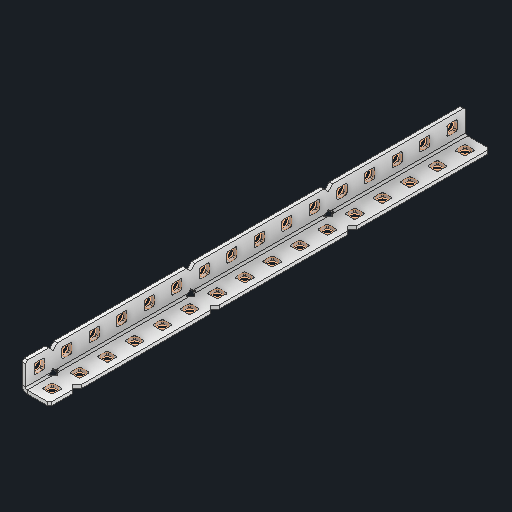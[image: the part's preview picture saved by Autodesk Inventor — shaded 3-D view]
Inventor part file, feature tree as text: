
AUTODESK INVENTOR PART (.ipt)
format: ipt  version: 2025 (Build 290162000, 162)  size: 732,160 bytes
history: native  units: in
note: dims shown in document units (in); Inventor stores cm internally (conversion verified against a paired STEP export)
features: other x73, sketch x2, sheet_metal_op x1
ambient origin geometry x8: Origin, YZ Plane, XZ Plane, XY Plane, X Axis, Y Axis, Z Axis, Center Point
bodies: Solid1 (feature_tree)
feature tree (76):
  other  "Alu Angle 1x1x16.ipt"
  other  "Solid1::Alu Angle 1x1x16.ipt"
  other  "TaggingFeature1"
  sketch  "Sketch1"  dims[d0=0.3937in]
  sketch  "Sketch2"  dims[d1=0.0625in]
  sheet_metal_op  "Body Pattern Sketch"
  other  "Arc Length"
  other  "Diagonal Plane"
  other  "Srf1"
  other  "Srf2"
  other  "Srf3"
  other  "Srf4"
  other  "Srf5"
  other  "Srf6"
  other  "Srf7"
  other  "Srf8"
  other  "Srf9"
  other  "Srf10"
  other  "Srf11"
  other  "Srf12"
  other  "Srf13"
  other  "Srf14"
  other  "Srf15"
  other  "Srf16"
  other  "Srf17"
  other  "Srf18"
  other  "Srf19"
  other  "Srf20"
  other  "Srf21"
  other  "Srf22"
  other  "Srf23"
  other  "Srf24"
  other  "Srf25"
  other  "Srf26"
  other  "Srf27"
  other  "Srf28"
  other  "Srf29"
  other  "Srf30"
  other  "Srf31"
  other  "Srf32"
  other  "Srf33"
  other  "Srf34"
  other  "Srf91::Derived"
  other  "Srf92::Derived"
  other  "Srf856::Derived"
  other  "Srf857::Derived"
  other  "Srf858::Derived"
  other  "Srf859::Derived"
  other  "Srf860::Derived"
  other  "Srf861::Derived"
  other  "Srf1383::Derived"
  other  "Srf1384::Derived"
  other  "Srf1385::Derived"
  other  "Srf1386::Derived"
  other  "Srf1387::Derived"
  other  "Srf1388::Derived"
  other  "Srf1389::Derived"
  other  "Srf1390::Derived"
  other  "Srf1391::Derived"
  other  "Srf1275::Derived"
  other  "Srf1276::Derived"
  other  "Srf1278::Derived"
  other  "Srf1279::Derived"
  other  "Srf1280::Derived"
  other  "Srf1281::Derived"
  other  "Srf1282::Derived"
  other  "Srf1283::Derived"
  other  "Srf1475::Derived"
  other  "Srf1476::Derived"
  other  "Srf1477::Derived"
  other  "Srf1478::Derived"
  other  "Srf1479::Derived"
  other  "Srf1480::Derived"
  other  "Srf1481::Derived"
  other  "Srf1482::Derived"
  other  "Srf1483::Derived"
